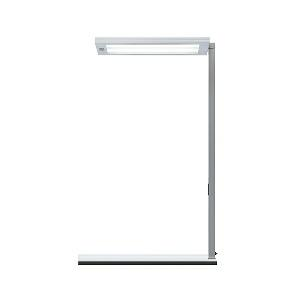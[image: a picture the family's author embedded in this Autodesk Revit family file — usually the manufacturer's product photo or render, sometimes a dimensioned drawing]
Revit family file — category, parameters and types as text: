
# Revit family: lavigo_-_dpt_12000_840_r_g2_00804498_5f82
name_source: partatom
category: Lighting Fixtures
units: mm (PartAtom-declared; Revit-internal decimal feet)

## family parameters
Cut with Voids When Loaded = No
Host = Face
Light Source = No
Part Type = Normal
Room Calculation Point = No
Round Connector Dimension = Use Diameter
Shared = No

## types (1)
- LAVIGO - DPT 12000/840/R/G2 (1 x LED, 11650 lm, 4000K)
    Apparent Load = 77 VA
    Approval mark = CE
    CIE Flux Codes = 60 87 97 15 100
    Color Rendering = 80-89
    Color Temperature = 4000K
    Control Gear = Electronic ballast
    Default Elevation = 1800 mm
    Description = DPT 12000/840/R/G2|Desk-mounted luminaire|light source: LED|work equipment: Electronic ballast|connected load: 220-240 V, 50/60 Hz|Power consumption: approx. 77 W|standby: approx. 0,50|power factor: approx. 0,930|luminous flux: 11650 lm|luminous efficacy: 151 lm/W|light distribution: Direct/indirect|direct ratio: approx. 15 %|colour temperature: Cold white, ca. 4000 K|color rendering index (CRI): >= 80|chromaticity tolerance:  3 SDCM|technology: Presence and daylight sensor control (PIR)|operation: Multi-function switch|luminaire body|material: Steel/plastic|surface: Painted|colour: Silver metallic|lamp cover: Acrylic (PMMA), Satine|tubular section|material: Steel tube|surface: Painted|Form: Tubular section upright|colour of tubular section: Silver metallic|weight (net): approx. 9.5 kg|mains lead: 3.70 m Mains plug CEE 7/VII|Fastening: Socket, Table adaptor|decorative contrast side parts: Flint grey|glare control: Prism aperture|luminance(L65): <= 3000 cd/m|unified glare rating(4H 8H): <=  16|special features: Luminaire head detachable, Cradle to Cradle Certified TM, Direct light component with edge light and light-guide technology for homogenous light exit, Flicker-free, Integrated light and presence sensor PIR, Retrofittable with TALK module, Inclination of tubular section adjustable, Separated, direct and indirect light individually adjustable|Approval mark: VDE - ENEC|
    Frequency = 50 Hz, 60 Hz
    Height = 36 mm
    Lamp = 1 x LED
    Lamp Light Flux = 11650 lm
    Lamp count = 1
    Length = 675 mm
    Luminous efficacy = 151 lm/W
    Manufacturer = Waldmann
    ModVariant = No
    Model = 00804498
    Mounting Place = Table
    Mounting Type = Surface mounted
    Number of Poles = 1
    OnlyDefault = Yes
    Power Factor = 1
    Product Name = LAVIGO - DPT 12000/840/R/G2
    Product group = Desk mounted luminaire with detector
    ProductGroupID = 2201
    Protection Class = Protection class I
    Protection Degree = IP 20
    RLX_Detail_Level = 1
    RLX_Emergency_Light_Flux = 0 lm
    RLX_Emergency_Type = 0
    RLX_Emergency_Type_DB = No
    RlxData = <blob elided: 35625 chars, md5=84d8cfd3>
    Socket = socket
    Standby Power = 0 W
    System Light Flux = 11650 lm
    System Power = 77 W
    Type Comments = Product without accessories
    Type Image = 121716000-00666945.jpg
    URL = http://relux.com
    VarID = ---
    Voltage = 230 V
    Voltage Range = 220-240 V
    Weight = 0.00 kg
    Width = 320 mm

## geometry (parser evidence)
native form markers: Blend x4, Sweep x13
no freeform markers — native parametric forms only
